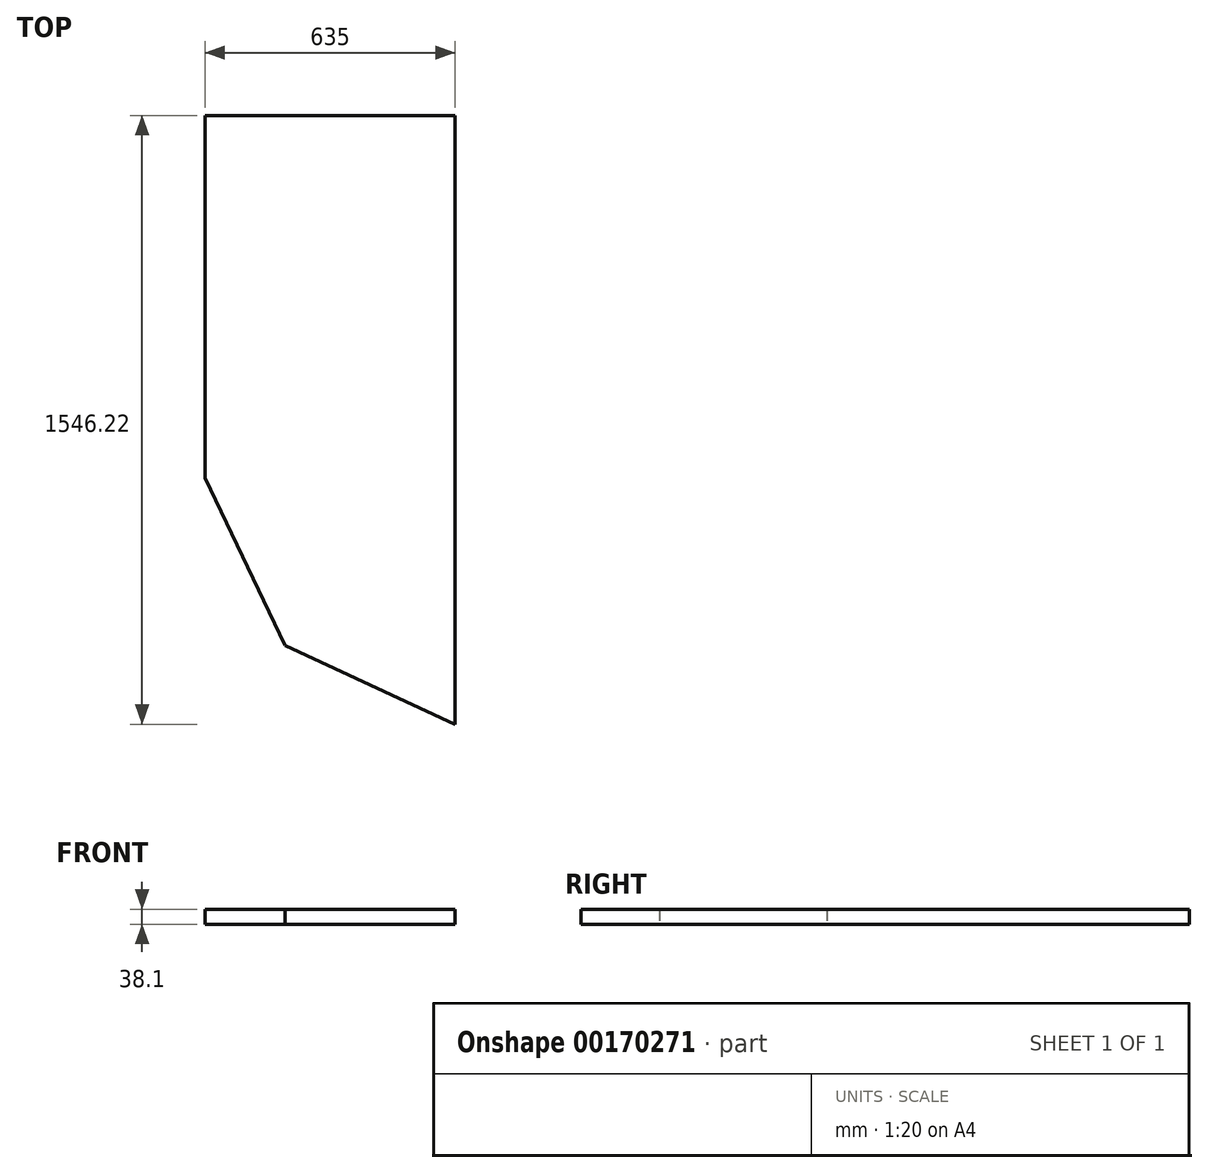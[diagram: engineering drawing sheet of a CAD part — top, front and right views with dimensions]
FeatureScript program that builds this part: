
annotation { "Feature Type Name" : "Feature", "Feature Type Description" : "" }
export const myFeature = defineFeature(function(context is Context, id is Id, definition is map)
    precondition{}
    {
        {
            var Q0;
            Q0=qCreatedBy(makeId("Top.planeOp"),FACE);
            var sketch = newSketch(context, id + "F0", { "sketchPlane" : qUnion([Q0])});
            skLineSegment(sketch, "E0", {"start": v(0, 0) * mm, "end": v(635, 0) * mm});
            skLineSegment(sketch, "E1", {"start": v(0, 0) * mm, "end": v(0, -635) * mm});
            skLineSegment(sketch, "E2", {"start": v(0, -635) * mm, "end": v(0, -920.75) * mm});
            skLineSegment(sketch, "E3", {"start": v(635, 0) * mm, "end": v(635, -1546.23) * mm});
            skLineSegment(sketch, "E4", {"start": v(203.2, -1346.2) * mm, "end": v(635, -1346.2) * mm, "construction": true});
            skLineSegment(sketch, "E5", {"start": v(635, -1546.23) * mm, "end": v(203.2, -1346.2) * mm});
            skLineSegment(sketch, "E6", {"start": v(0, -920.75) * mm, "end": v(203.2, -1346.2) * mm});
            skSolve(sketch);
        }
        {
            var Q0;
            Q0 = qSketchRegion(id + "F0", true);
            extrude(context, id + "F1", {"entities" : qUnion([Q0]), "depth" : 38.1 * mm});
        }
    });
